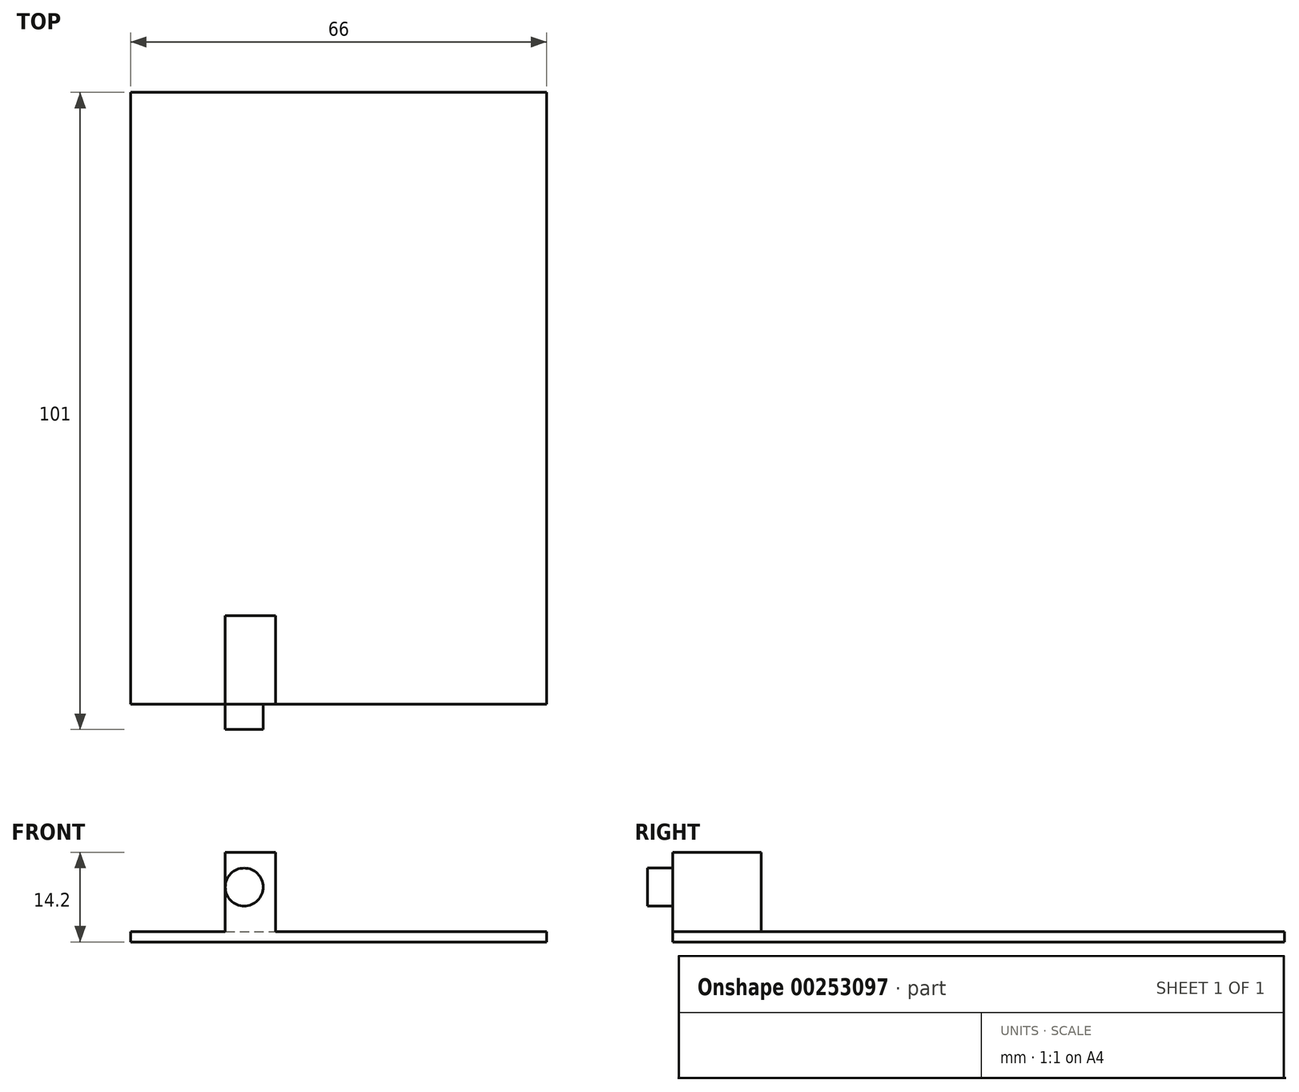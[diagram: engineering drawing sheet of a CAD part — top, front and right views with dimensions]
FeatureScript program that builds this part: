
annotation { "Feature Type Name" : "Feature", "Feature Type Description" : "" }
export const myFeature = defineFeature(function(context is Context, id is Id, definition is map)
    precondition{}
    {
        {
            var Q0;
            Q0=qCreatedBy(makeId("Top.planeOp"),FACE);
            var sketch = newSketch(context, id + "F0", { "sketchPlane" : qUnion([Q0])});
            skLineSegment(sketch, "E0.bottom", {"start": v(-33, 97) * mm, "end": v(33, 97) * mm});
            skLineSegment(sketch, "E0.top", {"start": v(-33, 0) * mm, "end": v(33, 0) * mm});
            skLineSegment(sketch, "E0.left", {"start": v(-33, 97) * mm, "end": v(-33, 0) * mm});
            skLineSegment(sketch, "E0.right", {"start": v(33, 97) * mm, "end": v(33, 0) * mm});
            skSolve(sketch);
        }
        {
            var Q0;
            Q0=makeQuery(id+"F0.imprint","IMPRINT",FACE,{"disambiguationData":[TD([[makeQuery(id+"F0.imprint","IMPRINT",EDGE,{"derivedFrom":sQuery(id+"F0.wireOp",EDGE,"E0.bottom")}),-1.0]])]});
            extrude(context, id + "F1", {"entities" : qUnion([Q0]), "depth" : 1.6 * mm});
        }
        {
            var Q0;
            Q0=makeQuery(id+"F1.opExtrude","CAP_FACE",FACE,{"disambiguationData":[OSD([sQuery(id+"F0.wireOp",EDGE,"E0.bottom"),sQuery(id+"F0.wireOp",EDGE,"E0.top"),sQuery(id+"F0.wireOp",EDGE,"E0.left"),sQuery(id+"F0.wireOp",EDGE,"E0.right")])],"isStart":false});
            var sketch = newSketch(context, id + "F2", { "sketchPlane" : qUnion([Q0])});
            skLineSegment(sketch, "E1.bottom", {"start": v(-18, 14) * mm, "end": v(-10, 14) * mm});
            skLineSegment(sketch, "E1.top", {"start": v(-18, 0) * mm, "end": v(-10, 0) * mm});
            skLineSegment(sketch, "E1.left", {"start": v(-18, 14) * mm, "end": v(-18, 0) * mm});
            skLineSegment(sketch, "E1.right", {"start": v(-10, 14) * mm, "end": v(-10, 0) * mm});
            skSolve(sketch);
        }
        {
            var Q0;
            Q0=makeQuery(id+"F2.imprint","IMPRINT",FACE,{"disambiguationData":[TD([[makeQuery(id+"F2.imprint","IMPRINT",EDGE,{"derivedFrom":sQuery(id+"F2.wireOp",EDGE,"E1.bottom")}),-1.0]])]});
            extrude(context, id + "F3", {"entities" : qUnion([Q0]), "operationType" : NewBodyOperationType.ADD, "depth" : 12.6 * mm});
        }
        {
            var Q0;
            Q0=makeQuery(id+"F3.boolean.opBoolean","MERGE",FACE,{"derivedFrom":[makeQuery(id+"F1.opExtrude","SWEPT_FACE",FACE,{"disambiguationData":[OSD([sQuery(id+"F0.wireOp",EDGE,"E0.top")])]}),makeQuery(id+"F3.opExtrude","SWEPT_FACE",FACE,{"disambiguationData":[OSD([sQuery(id+"F2.wireOp",EDGE,"E1.top")])]})]});
            var sketch = newSketch(context, id + "F4", { "sketchPlane" : qUnion([Q0])});
            skCircle(sketch, "E2", {"center": v(-15, 8.7) * mm, "radius": 3 * mm});
            skPoint(sketch, "E2.centerSnap0", {"position": v(-18, 8.7) * mm});
            skSolve(sketch);
        }
        {
            var Q0;
            Q0=makeQuery(id+"F4.imprint","IMPRINT",FACE,{"disambiguationData":[TD([[makeQuery(id+"F4.imprint","IMPRINT",EDGE,{"derivedFrom":sQuery(id+"F4.wireOp",EDGE,"E2")}),1.0]])]});
            extrude(context, id + "F5", {"entities" : qUnion([Q0]), "operationType" : NewBodyOperationType.ADD, "depth" : 4 * mm});
        }
    });
